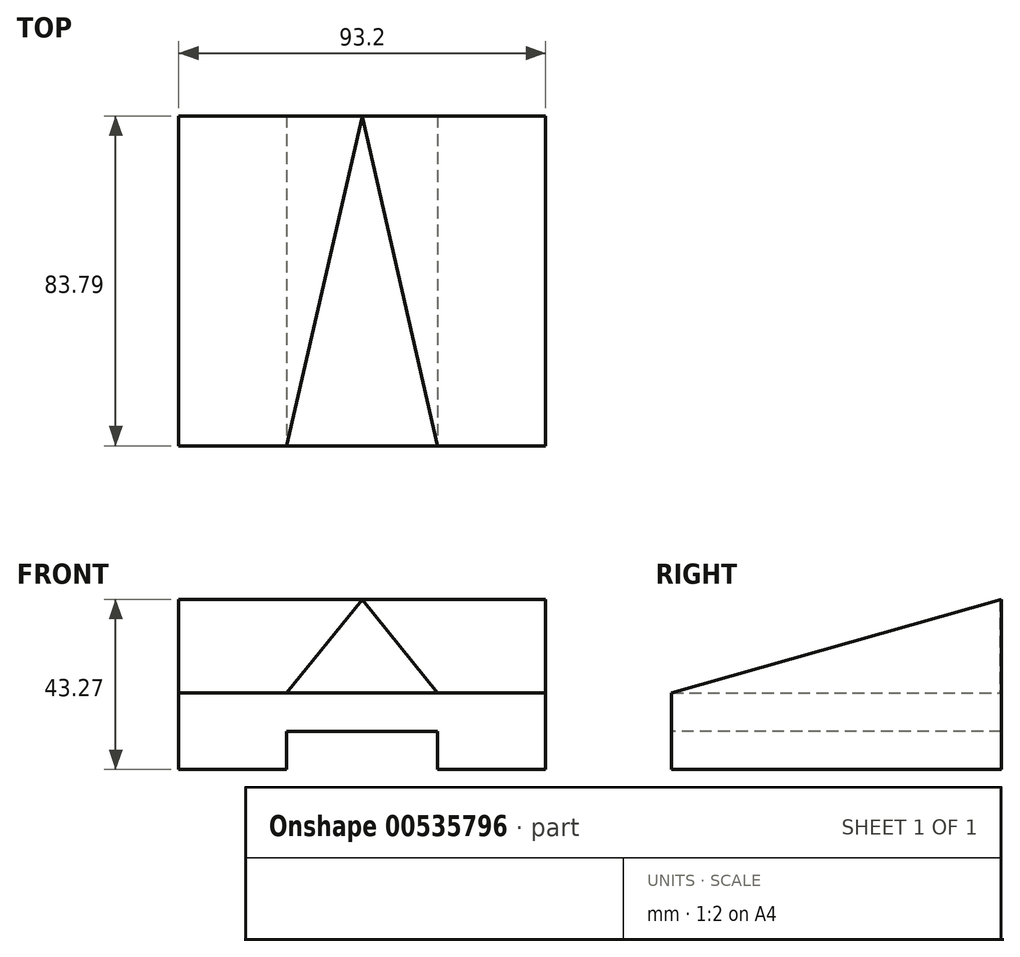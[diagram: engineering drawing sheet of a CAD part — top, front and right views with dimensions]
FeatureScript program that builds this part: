
annotation { "Feature Type Name" : "Feature", "Feature Type Description" : "" }
export const myFeature = defineFeature(function(context is Context, id is Id, definition is map)
    precondition{}
    {
        {
            var Q0;
            Q0=qCreatedBy(makeId("Right.planeOp"),FACE);
            var sketch = newSketch(context, id + "F0", { "sketchPlane" : qUnion([Q0])});
            skLineSegment(sketch, "E0", {"start": v(0, 0) * mm, "end": v(0, 19.46) * mm});
            skLineSegment(sketch, "E1", {"start": v(0, 19.46) * mm, "end": v(83.79, 43.27) * mm});
            skLineSegment(sketch, "E2", {"start": v(83.79, 43.27) * mm, "end": v(83.79, 0) * mm});
            skLineSegment(sketch, "E3", {"start": v(83.79, 0) * mm, "end": v(0, 0) * mm});
            skSolve(sketch);
        }
        {
            var Q0;
            Q0=makeQuery(id+"F0.imprint","IMPRINT",FACE,{"disambiguationData":[TD([[makeQuery(id+"F0.imprint","IMPRINT",EDGE,{"derivedFrom":sQuery(id+"F0.wireOp",EDGE,"E0")}),-1.0]])]});
            extrude(context, id + "F1", {"entities" : qUnion([Q0]), "endBound" : BoundingType.SYMMETRIC, "depth" : 93.2 * mm, "offsetDistance" : 25 * mm});
        }
        {
            var Q0;
            Q0=makeQuery(id+"F1.opExtrude","SWEPT_FACE",FACE,{"disambiguationData":[OSD([sQuery(id+"F0.wireOp",EDGE,"E0")])]});
            var sketch = newSketch(context, id + "F2", { "sketchPlane" : qUnion([Q0])});
            skLineSegment(sketch, "E4", {"start": v(0, 0) * mm, "end": v(0, 19.46) * mm, "construction": true});
            skPoint(sketch, "E5.oppositeSnap0", {"position": v(0, 9.73) * mm});
            skLineSegment(sketch, "E5.bottom", {"start": v(-19.18, 0) * mm, "end": v(19.18, 0) * mm});
            skLineSegment(sketch, "E5.top", {"start": v(-19.18, 9.73) * mm, "end": v(19.18, 9.73) * mm});
            skLineSegment(sketch, "E5.left", {"start": v(-19.18, 0) * mm, "end": v(-19.18, 9.73) * mm});
            skLineSegment(sketch, "E5.right", {"start": v(19.18, 0) * mm, "end": v(19.18, 9.73) * mm});
            skSolve(sketch);
        }
        {
            var Q0;
            Q0=makeQuery(id+"F2.imprint","IMPRINT",FACE,{"disambiguationData":[TD([[makeQuery(id+"F2.imprint","IMPRINT",EDGE,{"derivedFrom":sQuery(id+"F2.wireOp",EDGE,"E5.bottom")}),-1.0]])]});
            extrude(context, id + "F3", {"entities" : qUnion([Q0]), "operationType" : NewBodyOperationType.REMOVE, "endBound" : BoundingType.THROUGH_ALL, "oppositeDirection" : true, "depth" : 25 * mm, "offsetDistance" : 25 * mm});
        }
        {
            var Q0;
            Q0=qCreatedBy(makeId("Top.planeOp"),FACE);
            var Q1;
            Q1=makeQuery(id+"F1.opExtrude","CAP_VERTEX",VERTEX,{"disambiguationData":[OSD([sQuery(id+"F0.wireOp",EDGE,"E0"),sQuery(id+"F0.wireOp",EDGE,"E1")])],"isStart":false});
            cPlane(context, id + "F4", {"entities" : qUnion([Q0, Q1]), "cplaneType" : CPlaneType.PLANE_POINT, "offset" : 25 * mm, "width" : 150 * mm, "height" : 150 * mm});
        }
        {
            var Q0;
            Q0=qCreatedBy(id+"F4.planeOp",FACE);
            var sketch = newSketch(context, id + "F5", { "sketchPlane" : qUnion([Q0])});
            skLineSegment(sketch, "E6.0", {"start": v(19.18, 0) * mm, "end": v(-19.18, 0) * mm});
            skPoint(sketch, "E7.0", {"position": v(19.18, 0) * mm});
            skPoint(sketch, "E8.0", {"position": v(-19.18, 0) * mm});
            skLineSegment(sketch, "E9.0", {"start": v(46.6, 83.79) * mm, "end": v(-46.6, 83.79) * mm, "construction": true});
            skPoint(sketch, "E10.orphan", {"position": v(-46.6, 0) * mm});
            skPoint(sketch, "E11.orphan", {"position": v(46.6, 0) * mm});
            skLineSegment(sketch, "E12", {"start": v(0, 0) * mm, "end": v(0, 83.79) * mm, "construction": true});
            skLineSegment(sketch, "E13", {"start": v(-19.18, 0) * mm, "end": v(-0.1, 83.36) * mm});
            skLineSegment(sketch, "E14", {"start": v(19.18, 0) * mm, "end": v(0.1, 83.36) * mm});
            skPoint(sketch, "E15.visualSharp", {"position": v(0, 83.79) * mm});
            skArc(sketch, "E15.filletArc", {"start": v(0.1, 83.36) * mm, "mid": v(0, 83.44) * mm, "end": v(-0.1, 83.36) * mm});
            skSolve(sketch);
        }
        {
            var Q0;
            Q0 = qSketchRegion(id + "F5", true);
            extrude(context, id + "F6", {"entities" : qUnion([Q0]), "operationType" : NewBodyOperationType.REMOVE, "endBound" : BoundingType.THROUGH_ALL, "depth" : 25 * mm, "offsetDistance" : 25 * mm});
        }
    });
